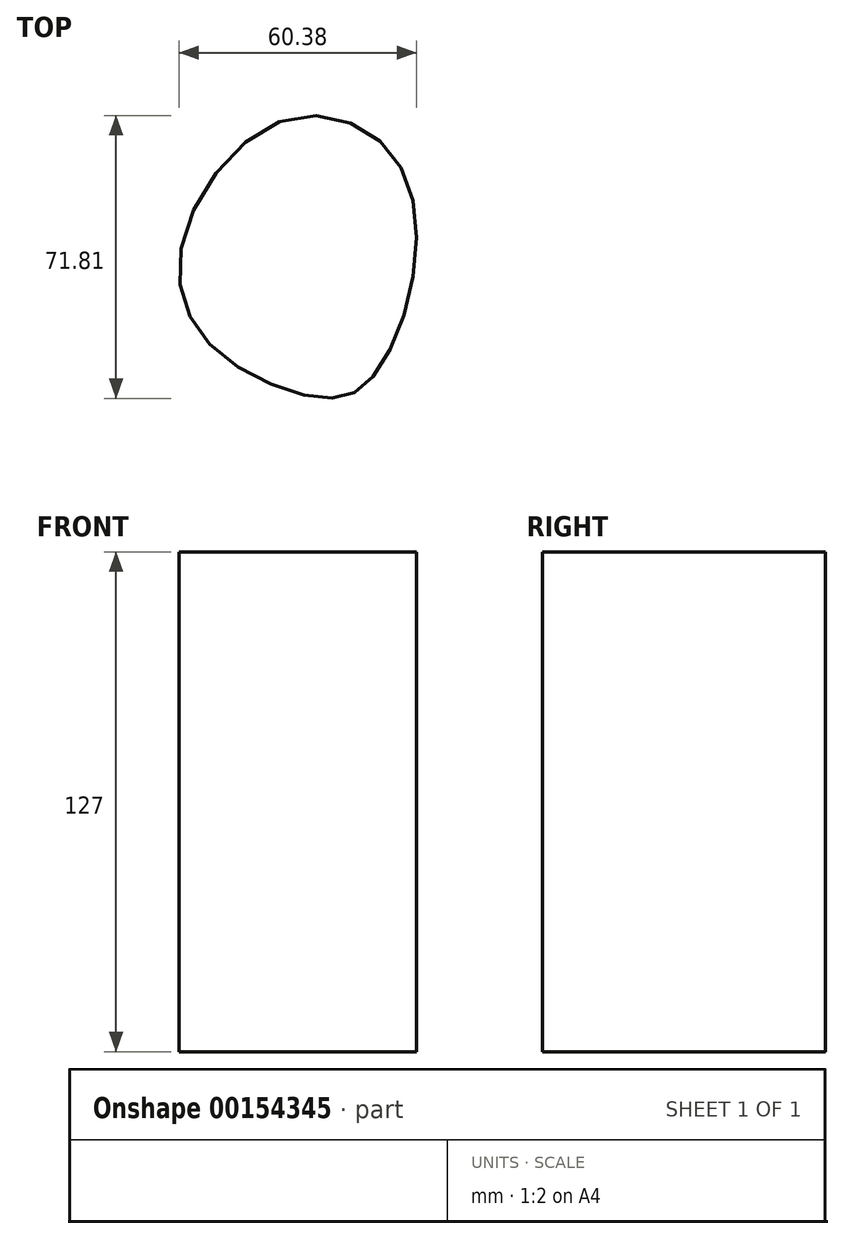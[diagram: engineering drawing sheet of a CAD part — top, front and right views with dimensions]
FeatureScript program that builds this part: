
annotation { "Feature Type Name" : "Feature", "Feature Type Description" : "" }
export const myFeature = defineFeature(function(context is Context, id is Id, definition is map)
    precondition{}
    {
        {
            var Q0;
            Q0=qCreatedBy(makeId("Top.planeOp"),FACE);
            var sketch = newSketch(context, id + "F0", { "sketchPlane" : qUnion([Q0])});
            skFitSpline(sketch, "E0", {"points": [v(-19.97, 45.07) * mm, v(7.34, 38.32) * mm, v(14.39, 8.66) * mm, v(2.94, -20.7) * mm, v(-9.69, -25.1) * mm, v(-36.7, -12.48) * mm, v(-44.92, 13.36) * mm, v(-19.97, 45.07) * mm]});
            skSolve(sketch);
        }
        {
            var Q0;
            Q0 = qSketchRegion(id + "F0", true);
            extrude(context, id + "F1", {"entities" : qUnion([Q0]), "depth" : 127 * mm});
        }
    });
